# Revit family: FP-Revit20-en-OS30NPTX1-CompactSteamOven-0-90003861A-US-CA
name_source: partatom
category: Generic Models
units: mm (PartAtom-declared; Revit-internal decimal feet)

## family parameters
Always vertical = Yes
Can host rebar = No
Cut with Voids When Loaded = No
Part Type = Normal
Room Calculation Point = No
Round Connector Dimension = Use Diameter
Shared = No
Work Plane-Based = No

## types (1)
- OS30NPTX1
    Cavity - Minimum Height = 446 mm  [stored 1.46325 ft]
    Cavity - minimum depth = 550 mm
    Cavity - minimum width = 724 mm  [stored 2.37533 ft]
    Chassis - Depth = 545 mm  [stored 1.78806 ft]
    Chassis - Height = 435 mm  [stored 1.42717 ft]
    Chassis - Width = 720 mm  [stored 2.3622 ft]
    Clearance - Door = Fisher & Paykel - Clearance Required
    Connector note = 208 or 240 V, 60 Hz, 20 A
    Default Elevation = 0 mm  [stored 0 ft]
    Description = Compact Steam Oven, 30"
    Manufacturer = Fisher & Paykel Appliances
    Material - Glass = Fisher & Paykel - Glass, Black
    Material - Handle = Fisher & Paykel - Stainless Steel
    Material - Stainless steel = Fisher & Paykel - Stainless Steel
    Model = OS30NPTX1
    Product - Overall depth (Excluding handle) = 575 mm
    Product - Overall height = 458 mm
    Product - Overall width = 757 mm  [stored 2.4836 ft]
    URL = www.fisherpaykel.com

note: [stored X ft] marks values corroborated as IEEE doubles in the binary element streams (Revit-internal decimal feet)

## geometry (parser evidence)
native form markers: Sweep x1
no freeform markers — native parametric forms only
